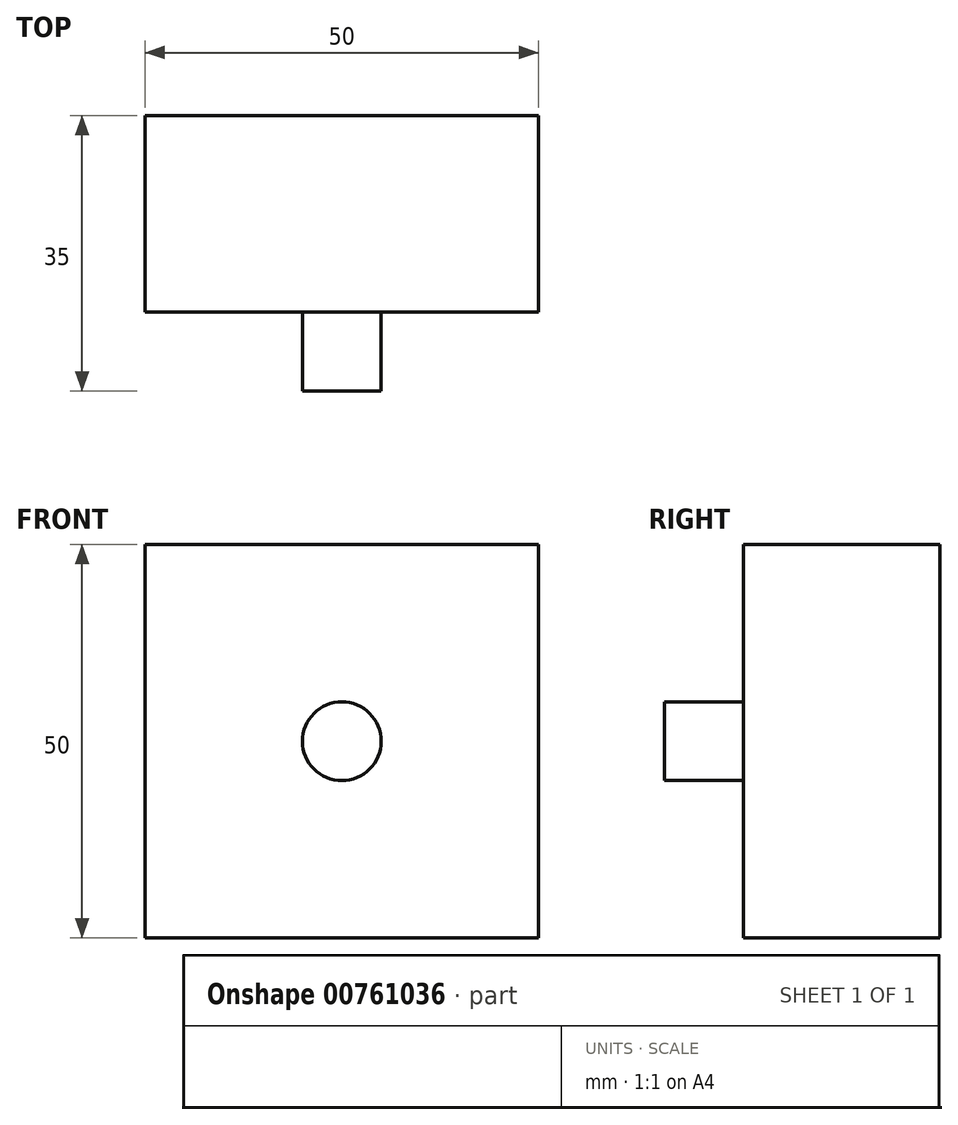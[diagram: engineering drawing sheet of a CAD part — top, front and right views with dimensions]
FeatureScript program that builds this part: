
annotation { "Feature Type Name" : "Feature", "Feature Type Description" : "" }
export const myFeature = defineFeature(function(context is Context, id is Id, definition is map)
    precondition{}
    {
        {
            var Q0;
            Q0=qCreatedBy(makeId("Front.planeOp"),FACE);
            var sketch = newSketch(context, id + "F0", { "sketchPlane" : qUnion([Q0])});
            skLineSegment(sketch, "E0.bottom", {"start": v(25, -25) * mm, "end": v(-25, -25) * mm});
            skLineSegment(sketch, "E0.top", {"start": v(25, 25) * mm, "end": v(-25, 25) * mm});
            skLineSegment(sketch, "E0.left", {"start": v(25, -25) * mm, "end": v(25, 25) * mm});
            skLineSegment(sketch, "E0.right", {"start": v(-25, -25) * mm, "end": v(-25, 25) * mm});
            skPoint(sketch, "E0.middle", {"position": v(0, 0) * mm});
            skSolve(sketch);
        }
        {
            var Q0;
            Q0=makeQuery(id+"F0.imprint","IMPRINT",FACE,{"disambiguationData":[TD([[makeQuery(id+"F0.imprint","IMPRINT",EDGE,{"derivedFrom":sQuery(id+"F0.wireOp",EDGE,"E0.bottom")}),-1.0]])]});
            extrude(context, id + "F1", {"entities" : qUnion([Q0]), "oppositeDirection" : true, "depth" : 25 * mm, "offsetDistance" : 25 * mm});
        }
        {
            var Q0;
            Q0=makeQuery(id+"F1.opExtrude","CAP_FACE",FACE,{"disambiguationData":[OSD([sQuery(id+"F0.wireOp",EDGE,"E0.bottom"),sQuery(id+"F0.wireOp",EDGE,"E0.top"),sQuery(id+"F0.wireOp",EDGE,"E0.left"),sQuery(id+"F0.wireOp",EDGE,"E0.right")])],"isStart":true});
            var sketch = newSketch(context, id + "F2", { "sketchPlane" : qUnion([Q0])});
            skCircle(sketch, "E1", {"center": v(0, 0) * mm, "radius": 5 * mm});
            skSolve(sketch);
        }
        {
            var Q0;
            Q0 = qSketchRegion(id + "F2", true);
            extrude(context, id + "F3", {"entities" : qUnion([Q0]), "operationType" : NewBodyOperationType.ADD, "depth" : 10 * mm, "offsetDistance" : 25 * mm});
        }
    });
